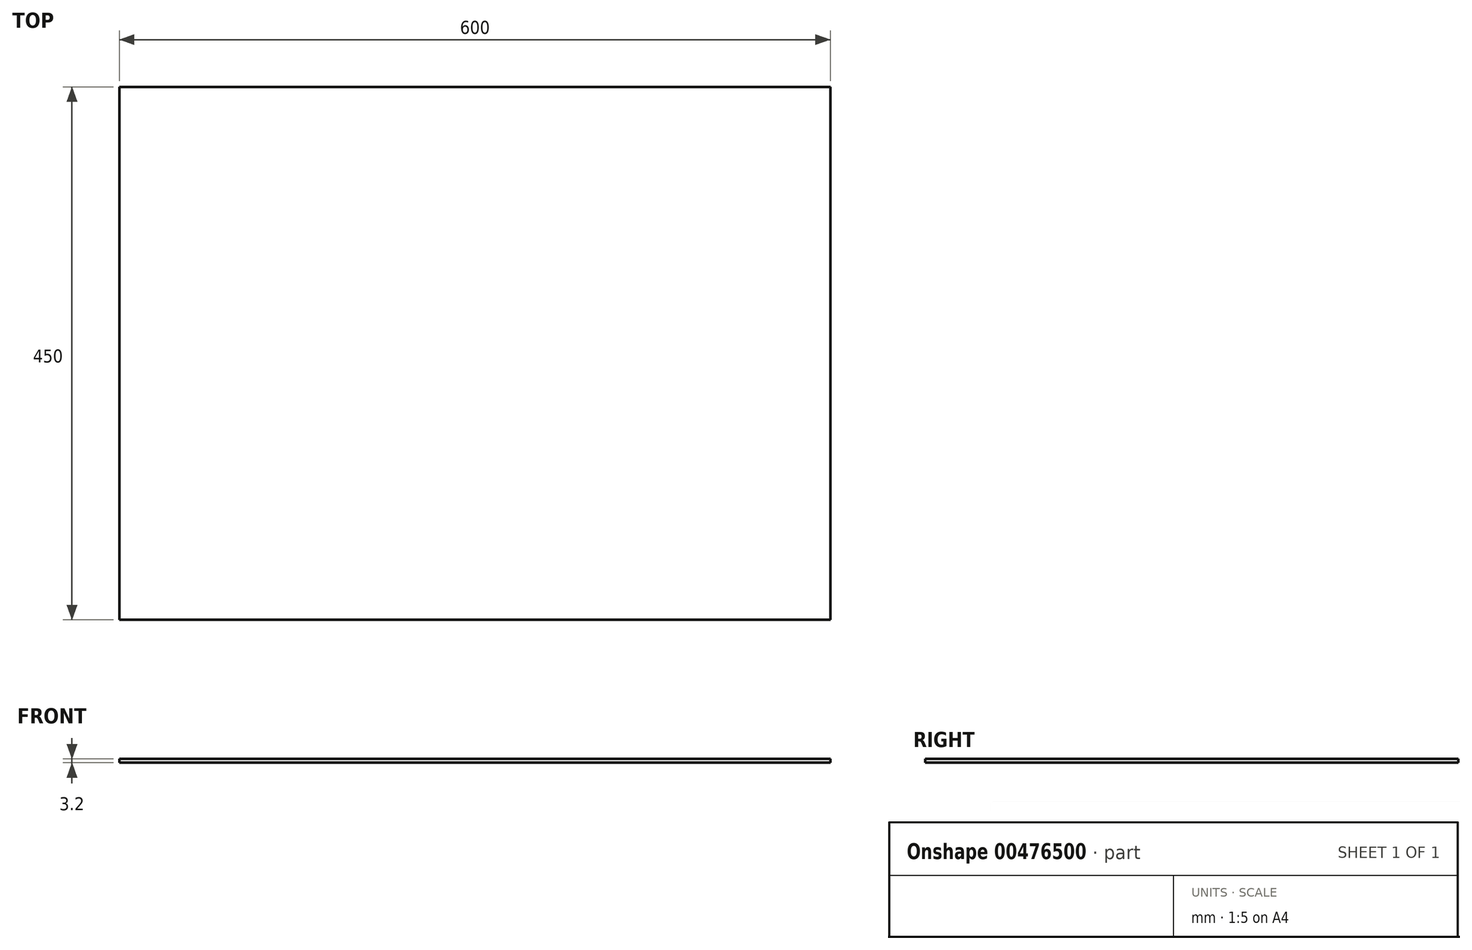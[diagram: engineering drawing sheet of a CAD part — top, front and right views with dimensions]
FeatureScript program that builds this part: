
annotation { "Feature Type Name" : "Feature", "Feature Type Description" : "" }
export const myFeature = defineFeature(function(context is Context, id is Id, definition is map)
    precondition{}
    {
        {
            var Q0;
            Q0=qCreatedBy(makeId("Top.planeOp"),FACE);
            var sketch = newSketch(context, id + "F0", { "sketchPlane" : qUnion([Q0])});
            skLineSegment(sketch, "E0.bottom", {"start": v(-226.15, 348.87) * mm, "end": v(373.85, 348.87) * mm});
            skLineSegment(sketch, "E0.top", {"start": v(-226.15, -101.13) * mm, "end": v(373.85, -101.13) * mm});
            skLineSegment(sketch, "E0.left", {"start": v(-226.15, 348.87) * mm, "end": v(-226.15, -101.13) * mm});
            skLineSegment(sketch, "E0.right", {"start": v(373.85, 348.87) * mm, "end": v(373.85, -101.13) * mm});
            skSolve(sketch);
        }
        {
            var Q0;
            Q0 = qSketchRegion(id + "F0", true);
            extrude(context, id + "F1", {"entities" : qUnion([Q0]), "depth" : 3.2 * mm, "offsetDistance" : 25 * mm});
        }
    });
